# Revit family: 872-00-001-DN80-1600
name_source: partatom
category: Pipe Accessories
units: mm (PartAtom-declared; Revit-internal decimal feet)

## family parameters
Always vertical = Yes
Cut with Voids When Loaded = No
Part Type = Valve - Breaks Into
Round Connector Dimension = Use Diameter
Shared = No
Work Plane-Based = No

## types (33) — shared parameters
Body_wallthickness = 10 mm  [stored 0.0328084 ft]
DN080_PN10/16 = 872-0080-00-10900100100
DN1000_PN10 = 872-1000-00-00100100000
DN1000_PN16 = 872-1000-00-10100100000
DN100_PN10/16 = 872-0100-00-10900100100
DN1200_PN10 = 872-1200-00-00100100000
DN1200_PN16 = 872-1200-00-10100100000
DN1400_PN10 = 872-1400-00-00100100000
DN1400_PN16 = 872-1400-00-10100100000
DN150_PN10/16 = 872-0150-00-10900100100
DN1600_PN10 = 872-1600-00-00100100000
DN1600_PN16 = 872-1600-00-10100100000
DN200_PN10 = 872-0200-00-00100100000
DN200_PN16 = 872-0200-00-10100100000
DN250_PN10 = 872-0250-00-00100100000
DN250_PN16 = 872-0250-00-10100100000
DN300_PN10 = 872-0300-00-00100100000
DN300_PN16 = 872-0300-00-10100100000
DN350_PN10 = 872-0350-00-00100100000
DN350_PN16 = 872-0350-00-10100100000
DN400_PN10 = 872-0400-00-00100100000
DN400_PN16 = 872-0400-00-10100100000
DN450_PN10 = 872-0450-00-00100100000
DN450_PN16 = 872-0450-00-10100100000
DN500_PN10 = 872-0500-00-00100100000
DN500_PN16 = 872-0500-00-10100100000
DN600_PN10 = 872-0600-00-00100100000
DN600_PN16 = 872-0600-00-10100100000
DN700_PN10 = 872-0700-00-00100100000
DN700_PN16 = 872-0700-00-10100100000
DN800_PN10 = 872-0800-00-00100100000
DN800_PN16 = 872-0800-00-10100100000
DN900_PN10 = 872-0900-00-00100100000
DN900_PN16 = 872-0900-00-10100100000
Description_ = AVK NEEDLE VALVE
RF_Thick = 3 mm  [stored 0.00984252 ft]
Search_Table = 872-00-001-DN80-1600
URL product pages = https://www.avkvalves.com

## per-type parameters (varying)
- DN0080_PN10/16: (A_ref+W)/2=303 mm; A=125 mm; A_ref=275 mm; B=117 mm; D=100 mm; DN=80 mm  [stored 0.262467 ft]; FOD=95 mm; FOD_ref=50 mm  [stored 0.164042 ft]; FOD_ref_2=32 mm  [stored 0.104987 ft]; Fillet_thickness=10 mm  [stored 0.0328084 ft]; Flange_thickness=19 mm  [stored 0.062336 ft]; Flange_thickness_ref=10 mm  [stored 0.0328084 ft]; Flange_thickness_ref_2=5 mm  [stored 0.0164042 ft]; H3=230 mm; H3_ref=195 mm; ID=40 mm  [stored 0.131234 ft]; ID_ref=70 mm  [stored 0.229659 ft]; ID_ref_2=35 mm  [stored 0.114829 ft]; ID_ref_3=105 mm; ID_ref_4=35 mm  [stored 0.114829 ft]; L=260 mm; L1=111 mm; L2=65 mm  [stored 0.213255 ft]; Rf_Dia=66 mm  [stored 0.216535 ft]; Ring_Dia=35 mm  [stored 0.114829 ft]; Ring_Dia_2=15 mm  [stored 0.0492126 ft]; W=330 mm
- DN0100_PN10/16: (A_ref+W)/2=334 mm; A=145 mm; A_ref=308 mm; B=117 mm; D=120 mm; DN=100 mm; FOD=110 mm; FOD_ref=60 mm  [stored 0.19685 ft]; FOD_ref_2=37 mm; Fillet_thickness=10 mm  [stored 0.0328084 ft]; Flange_thickness=19 mm  [stored 0.062336 ft]; Flange_thickness_ref=10 mm  [stored 0.0328084 ft]; Flange_thickness_ref_2=5 mm  [stored 0.0164042 ft]; H3=230 mm; H3_ref=195 mm; ID=50 mm  [stored 0.164042 ft]; ID_ref=70 mm  [stored 0.229659 ft]; ID_ref_2=35 mm  [stored 0.114829 ft]; ID_ref_3=105 mm; ID_ref_4=35 mm  [stored 0.114829 ft]; L=300 mm; L1=131 mm; L2=75 mm; Rf_Dia=78 mm  [stored 0.255906 ft]; Ring_Dia=35 mm  [stored 0.114829 ft]; Ring_Dia_2=15 mm  [stored 0.0492126 ft]; W=360 mm
- DN0150_PN10/16: (A_ref+W)/2=398 mm; A=175 mm; A_ref=371 mm; B=150 mm; D=135 mm; DN=150 mm; FOD=143 mm; FOD_ref=85 mm; FOD_ref_2=48 mm  [stored 0.15748 ft]; Fillet_thickness=10 mm  [stored 0.0328084 ft]; Flange_thickness=19 mm  [stored 0.062336 ft]; Flange_thickness_ref=10 mm  [stored 0.0328084 ft]; Flange_thickness_ref_2=5 mm  [stored 0.0164042 ft]; H3=295 mm; H3_ref=260 mm; ID=75 mm; ID_ref=70 mm  [stored 0.229659 ft]; ID_ref_2=35 mm  [stored 0.114829 ft]; ID_ref_3=105 mm; ID_ref_4=35 mm  [stored 0.114829 ft]; L=350 mm; L1=156 mm; L2=88 mm; Rf_Dia=106 mm; Ring_Dia=35 mm  [stored 0.114829 ft]; Ring_Dia_2=15 mm  [stored 0.0492126 ft]; W=425 mm
- DN0200_PN10: (A_ref+W)/2=473 mm; A=220 mm; A_ref=445 mm; B=150 mm; D=150 mm; DN=200 mm; FOD=170 mm; FOD_ref=110 mm; FOD_ref_2=57 mm; Fillet_thickness=20 mm  [stored 0.0656168 ft]; Flange_thickness=20 mm  [stored 0.0656168 ft]; Flange_thickness_ref=10 mm  [stored 0.0328084 ft]; Flange_thickness_ref_2=5 mm  [stored 0.0164042 ft]; H3=425 mm; H3_ref=380 mm; ID=100 mm; ID_ref=90 mm; ID_ref_2=45 mm  [stored 0.147638 ft]; ID_ref_3=135 mm; ID_ref_4=45 mm  [stored 0.147638 ft]; L=400 mm; L1=180 mm; L2=100 mm; Rf_Dia=133 mm; Ring_Dia=45 mm  [stored 0.147638 ft]; Ring_Dia_2=25 mm  [stored 0.082021 ft]; W=500 mm
- DN0200_PN16: (A_ref+W)/2=473 mm; A=220 mm; A_ref=445 mm; B=150 mm; D=150 mm; DN=200 mm; FOD=170 mm; FOD_ref=110 mm; FOD_ref_2=57 mm; Fillet_thickness=20 mm  [stored 0.0656168 ft]; Flange_thickness=20 mm  [stored 0.0656168 ft]; Flange_thickness_ref=10 mm  [stored 0.0328084 ft]; Flange_thickness_ref_2=5 mm  [stored 0.0164042 ft]; H3=425 mm; H3_ref=378 mm; ID=100 mm; ID_ref=95 mm; ID_ref_2=48 mm  [stored 0.15748 ft]; ID_ref_3=143 mm; ID_ref_4=48 mm  [stored 0.15748 ft]; L=400 mm; L1=180 mm; L2=100 mm; Rf_Dia=133 mm; Ring_Dia=48 mm  [stored 0.15748 ft]; Ring_Dia_2=28 mm  [stored 0.0918635 ft]; W=500 mm
- DN0250_PN10: (A_ref+W)/2=539 mm; A=260 mm; A_ref=513 mm; B=150 mm; D=165 mm; DN=250 mm; FOD=200 mm; FOD_ref=135 mm; FOD_ref_2=67 mm; Fillet_thickness=22 mm  [stored 0.0721785 ft]; Flange_thickness=22 mm  [stored 0.0721785 ft]; Flange_thickness_ref=11 mm  [stored 0.0360892 ft]; Flange_thickness_ref_2=6 mm  [stored 0.019685 ft]; H3=475 mm; H3_ref=415 mm; ID=125 mm; ID_ref=120 mm; ID_ref_2=60 mm  [stored 0.19685 ft]; ID_ref_3=180 mm; ID_ref_4=60 mm  [stored 0.19685 ft]; L=450 mm; L1=203 mm; L2=113 mm; Rf_Dia=160 mm; Ring_Dia=60 mm  [stored 0.19685 ft]; Ring_Dia_2=40 mm  [stored 0.131234 ft]; W=565 mm
- DN0250_PN16: (A_ref+W)/2=543 mm; A=260 mm; A_ref=515 mm; B=150 mm; D=165 mm; DN=250 mm; FOD=200 mm; FOD_ref=135 mm; FOD_ref_2=67 mm; Fillet_thickness=22 mm  [stored 0.0721785 ft]; Flange_thickness=22 mm  [stored 0.0721785 ft]; Flange_thickness_ref=11 mm  [stored 0.0360892 ft]; Flange_thickness_ref_2=6 mm  [stored 0.019685 ft]; H3=475 mm; H3_ref=415 mm; ID=125 mm; ID_ref=120 mm; ID_ref_2=60 mm  [stored 0.19685 ft]; ID_ref_3=180 mm; ID_ref_4=60 mm  [stored 0.19685 ft]; L=450 mm; L1=203 mm; L2=113 mm; Rf_Dia=160 mm; Ring_Dia=60 mm  [stored 0.19685 ft]; Ring_Dia_2=40 mm  [stored 0.131234 ft]; W=570 mm
- DN0300_PN10: (A_ref+W)/2=624 mm; A=305 mm; A_ref=594 mm; B=155 mm; D=185 mm; DN=300 mm; FOD=228 mm; FOD_ref=160 mm; FOD_ref_2=76 mm; Fillet_thickness=25 mm  [stored 0.082021 ft]; Flange_thickness=25 mm  [stored 0.082021 ft]; Flange_thickness_ref=12 mm  [stored 0.0393701 ft]; Flange_thickness_ref_2=6 mm  [stored 0.019685 ft]; H3=535 mm; H3_ref=470 mm; ID=150 mm; ID_ref=130 mm; ID_ref_2=65 mm  [stored 0.213255 ft]; ID_ref_3=195 mm; ID_ref_4=65 mm  [stored 0.213255 ft]; L=500 mm; L1=226 mm; L2=125 mm; Rf_Dia=185 mm; Ring_Dia=65 mm  [stored 0.213255 ft]; Ring_Dia_2=45 mm  [stored 0.147638 ft]; W=655 mm
- DN0300_PN16: (A_ref+W)/2=624 mm; A=305 mm; A_ref=594 mm; B=155 mm; D=185 mm; DN=300 mm; FOD=228 mm; FOD_ref=160 mm; FOD_ref_2=76 mm; Fillet_thickness=25 mm  [stored 0.082021 ft]; Flange_thickness=25 mm  [stored 0.082021 ft]; Flange_thickness_ref=12 mm  [stored 0.0393701 ft]; Flange_thickness_ref_2=6 mm  [stored 0.019685 ft]; H3=535 mm; H3_ref=470 mm; ID=150 mm; ID_ref=130 mm; ID_ref_2=65 mm  [stored 0.213255 ft]; ID_ref_3=195 mm; ID_ref_4=65 mm  [stored 0.213255 ft]; L=500 mm; L1=226 mm; L2=125 mm; Rf_Dia=185 mm; Ring_Dia=65 mm  [stored 0.213255 ft]; Ring_Dia_2=45 mm  [stored 0.147638 ft]; W=655 mm
- DN0350_PN10: (A_ref+W)/2=691 mm; A=345 mm; A_ref=663 mm; B=170 mm; D=205 mm; DN=350 mm; FOD=260 mm; FOD_ref=185 mm; FOD_ref_2=87 mm; Fillet_thickness=27 mm; Flange_thickness=27 mm; Flange_thickness_ref=13 mm; Flange_thickness_ref_2=7 mm  [stored 0.0229659 ft]; H3=595 mm; H3_ref=520 mm; ID=175 mm; ID_ref=150 mm; ID_ref_2=75 mm; ID_ref_3=225 mm; ID_ref_4=75 mm; L=550 mm; L1=249 mm; L2=138 mm; Rf_Dia=215 mm; Ring_Dia=75 mm; Ring_Dia_2=55 mm  [stored 0.180446 ft]; W=720 mm
- DN0350_PN16: (A_ref+W)/2=695 mm; A=345 mm; A_ref=665 mm; B=170 mm; D=205 mm; DN=350 mm; FOD=260 mm; FOD_ref=185 mm; FOD_ref_2=87 mm; Fillet_thickness=27 mm; Flange_thickness=27 mm; Flange_thickness_ref=13 mm; Flange_thickness_ref_2=7 mm  [stored 0.0229659 ft]; H3=595 mm; H3_ref=520 mm; ID=175 mm; ID_ref=150 mm; ID_ref_2=75 mm; ID_ref_3=225 mm; ID_ref_4=75 mm; L=550 mm; L1=249 mm; L2=138 mm; Rf_Dia=215 mm; Ring_Dia=75 mm; Ring_Dia_2=55 mm  [stored 0.180446 ft]; W=725 mm
- DN0400_PN10: (A_ref+W)/2=788 mm; A=385 mm; A_ref=750 mm; B=300 mm; D=235 mm; DN=400 mm; FOD=290 mm; FOD_ref=210 mm; FOD_ref_2=97 mm; Fillet_thickness=28 mm  [stored 0.0918635 ft]; Flange_thickness=28 mm  [stored 0.0918635 ft]; Flange_thickness_ref=14 mm  [stored 0.0459318 ft]; Flange_thickness_ref_2=7 mm  [stored 0.0229659 ft]; H3=660 mm; H3_ref=585 mm; ID=200 mm; ID_ref=150 mm; ID_ref_2=75 mm; ID_ref_3=225 mm; ID_ref_4=75 mm; L=600 mm; L1=272 mm; L2=150 mm; Rf_Dia=240 mm; Ring_Dia=75 mm; Ring_Dia_2=55 mm  [stored 0.180446 ft]; W=825 mm
- DN0400_PN16: (A_ref+W)/2=788 mm; A=385 mm; A_ref=750 mm; B=300 mm; D=235 mm; DN=400 mm; FOD=290 mm; FOD_ref=210 mm; FOD_ref_2=97 mm; Fillet_thickness=28 mm  [stored 0.0918635 ft]; Flange_thickness=28 mm  [stored 0.0918635 ft]; Flange_thickness_ref=14 mm  [stored 0.0459318 ft]; Flange_thickness_ref_2=7 mm  [stored 0.0229659 ft]; H3=660 mm; H3_ref=585 mm; ID=200 mm; ID_ref=150 mm; ID_ref_2=75 mm; ID_ref_3=225 mm; ID_ref_4=75 mm; L=600 mm; L1=272 mm; L2=150 mm; Rf_Dia=240 mm; Ring_Dia=75 mm; Ring_Dia_2=55 mm  [stored 0.180446 ft]; W=825 mm
- DN0450_PN10: (A_ref+W)/2=840 mm; A=415 mm; A_ref=805 mm; B=300 mm; D=240 mm; DN=450 mm; FOD=320 mm; FOD_ref=235 mm; FOD_ref_2=107 mm; Fillet_thickness=30 mm  [stored 0.0984252 ft]; Flange_thickness=30 mm  [stored 0.0984252 ft]; Flange_thickness_ref=15 mm  [stored 0.0492126 ft]; Flange_thickness_ref_2=8 mm  [stored 0.0262467 ft]; H3=745 mm; H3_ref=670 mm; ID=225 mm; ID_ref=150 mm; ID_ref_2=75 mm; ID_ref_3=225 mm; ID_ref_4=75 mm; L=650 mm; L1=295 mm; L2=163 mm; Rf_Dia=274 mm; Ring_Dia=75 mm; Ring_Dia_2=55 mm  [stored 0.180446 ft]; W=875 mm
- DN0450_PN16: (A_ref+W)/2=848 mm; A=415 mm; A_ref=810 mm; B=300 mm; D=240 mm; DN=450 mm; FOD=320 mm; FOD_ref=235 mm; FOD_ref_2=107 mm; Fillet_thickness=30 mm  [stored 0.0984252 ft]; Flange_thickness=30 mm  [stored 0.0984252 ft]; Flange_thickness_ref=15 mm  [stored 0.0492126 ft]; Flange_thickness_ref_2=8 mm  [stored 0.0262467 ft]; H3=745 mm; H3_ref=670 mm; ID=225 mm; ID_ref=150 mm; ID_ref_2=75 mm; ID_ref_3=225 mm; ID_ref_4=75 mm; L=650 mm; L1=295 mm; L2=163 mm; Rf_Dia=274 mm; Ring_Dia=75 mm; Ring_Dia_2=55 mm  [stored 0.180446 ft]; W=885 mm
- DN0500_PN10: (A_ref+W)/2=902 mm; A=445 mm; A_ref=869 mm; B=300 mm; D=245 mm; DN=500 mm; FOD=358 mm; FOD_ref=260 mm; FOD_ref_2=119 mm; Fillet_thickness=32 mm  [stored 0.104987 ft]; Flange_thickness=32 mm  [stored 0.104987 ft]; Flange_thickness_ref=16 mm; Flange_thickness_ref_2=8 mm  [stored 0.0262467 ft]; H3=785 mm; H3_ref=710 mm; ID=250 mm; ID_ref=150 mm; ID_ref_2=75 mm; ID_ref_3=225 mm; ID_ref_4=75 mm; L=700 mm; L1=319 mm; L2=175 mm; Rf_Dia=291 mm; Ring_Dia=75 mm; Ring_Dia_2=55 mm  [stored 0.180446 ft]; W=935 mm
- DN0500_PN16: (A_ref+W)/2=913 mm; A=445 mm; A_ref=876 mm; B=300 mm; D=245 mm; DN=500 mm; FOD=358 mm; FOD_ref=260 mm; FOD_ref_2=119 mm; Fillet_thickness=32 mm  [stored 0.104987 ft]; Flange_thickness=32 mm  [stored 0.104987 ft]; Flange_thickness_ref=16 mm; Flange_thickness_ref_2=8 mm  [stored 0.0262467 ft]; H3=785 mm; H3_ref=710 mm; ID=250 mm; ID_ref=150 mm; ID_ref_2=75 mm; ID_ref_3=225 mm; ID_ref_4=75 mm; L=700 mm; L1=319 mm; L2=175 mm; Rf_Dia=291 mm; Ring_Dia=75 mm; Ring_Dia_2=55 mm  [stored 0.180446 ft]; W=950 mm
- DN0600_PN10: (A_ref+W)/2=1026 mm; A=505 mm; A_ref=993 mm; B=300 mm; D=280 mm; DN=600 mm; FOD=420 mm; FOD_ref=310 mm; FOD_ref_2=140 mm; Fillet_thickness=36 mm  [stored 0.11811 ft]; Flange_thickness=36 mm  [stored 0.11811 ft]; Flange_thickness_ref=18 mm  [stored 0.0590551 ft]; Flange_thickness_ref_2=9 mm  [stored 0.0295276 ft]; H3=925 mm; H3_ref=845 mm; ID=300 mm; ID_ref=160 mm; ID_ref_2=80 mm  [stored 0.262467 ft]; ID_ref_3=240 mm; ID_ref_4=80 mm  [stored 0.262467 ft]; L=800 mm; L1=364 mm; L2=200 mm; Rf_Dia=360 mm; Ring_Dia=80 mm  [stored 0.262467 ft]; Ring_Dia_2=60 mm  [stored 0.19685 ft]; W=1060 mm
- DN0600_PN16: (A_ref+W)/2=1034 mm; A=505 mm; A_ref=998 mm; B=300 mm; D=280 mm; DN=600 mm; FOD=420 mm; FOD_ref=310 mm; FOD_ref_2=140 mm; Fillet_thickness=36 mm  [stored 0.11811 ft]; Flange_thickness=36 mm  [stored 0.11811 ft]; Flange_thickness_ref=18 mm  [stored 0.0590551 ft]; Flange_thickness_ref_2=9 mm  [stored 0.0295276 ft]; H3=925 mm; H3_ref=845 mm; ID=300 mm; ID_ref=160 mm; ID_ref_2=80 mm  [stored 0.262467 ft]; ID_ref_3=240 mm; ID_ref_4=80 mm  [stored 0.262467 ft]; L=800 mm; L1=364 mm; L2=200 mm; Rf_Dia=360 mm; Ring_Dia=80 mm  [stored 0.262467 ft]; Ring_Dia_2=60 mm  [stored 0.19685 ft]; W=1070 mm
- DN0700_PN10: (A_ref+W)/2=1142 mm; A=565 mm; A_ref=1099 mm; B=305 mm; D=315 mm; DN=700 mm; FOD=448 mm; FOD_ref=360 mm; FOD_ref_2=149 mm; Fillet_thickness=40 mm  [stored 0.131234 ft]; Flange_thickness=40 mm  [stored 0.131234 ft]; Flange_thickness_ref=20 mm  [stored 0.0656168 ft]; Flange_thickness_ref_2=10 mm  [stored 0.0328084 ft]; H3=1045 mm; H3_ref=965 mm; ID=350 mm; ID_ref=160 mm; ID_ref_2=80 mm  [stored 0.262467 ft]; ID_ref_3=240 mm; ID_ref_4=80 mm  [stored 0.262467 ft]; L=900 mm; L1=410 mm; L2=225 mm; Rf_Dia=397 mm; Ring_Dia=80 mm  [stored 0.262467 ft]; Ring_Dia_2=60 mm  [stored 0.19685 ft]; W=1185 mm
- DN0700_PN16: (A_ref+W)/2=1144 mm; A=565 mm; A_ref=1103 mm; B=305 mm; D=315 mm; DN=700 mm; FOD=455 mm; FOD_ref=360 mm; FOD_ref_2=152 mm; Fillet_thickness=40 mm  [stored 0.131234 ft]; Flange_thickness=40 mm  [stored 0.131234 ft]; Flange_thickness_ref=20 mm  [stored 0.0656168 ft]; Flange_thickness_ref_2=10 mm  [stored 0.0328084 ft]; H3=1045 mm; H3_ref=965 mm; ID=350 mm; ID_ref=160 mm; ID_ref_2=80 mm  [stored 0.262467 ft]; ID_ref_3=240 mm; ID_ref_4=80 mm  [stored 0.262467 ft]; L=900 mm; L1=410 mm; L2=225 mm; Rf_Dia=397 mm; Ring_Dia=80 mm  [stored 0.262467 ft]; Ring_Dia_2=60 mm  [stored 0.19685 ft]; W=1185 mm
- DN0800_PN10: (A_ref+W)/2=1291 mm; A=650 mm; A_ref=1246 mm; B=305 mm; D=350 mm; DN=800 mm; FOD=508 mm; FOD_ref=410 mm; FOD_ref_2=169 mm; Fillet_thickness=40 mm  [stored 0.131234 ft]; Flange_thickness=40 mm  [stored 0.131234 ft]; Flange_thickness_ref=20 mm  [stored 0.0656168 ft]; Flange_thickness_ref_2=10 mm  [stored 0.0328084 ft]; H3=1180 mm; H3_ref=1100 mm; ID=400 mm; ID_ref=160 mm; ID_ref_2=80 mm  [stored 0.262467 ft]; ID_ref_3=240 mm; ID_ref_4=80 mm  [stored 0.262467 ft]; L=1000 mm; L1=460 mm; L2=250 mm; Rf_Dia=450 mm; Ring_Dia=80 mm  [stored 0.262467 ft]; Ring_Dia_2=60 mm  [stored 0.19685 ft]; W=1335 mm
- DN0800_PN16: (A_ref+W)/2=1291 mm; A=650 mm; A_ref=1246 mm; B=335 mm; D=350 mm; DN=801 mm; FOD=508 mm; FOD_ref=411 mm; FOD_ref_2=169 mm; Fillet_thickness=40 mm  [stored 0.131234 ft]; Flange_thickness=40 mm  [stored 0.131234 ft]; Flange_thickness_ref=20 mm  [stored 0.0656168 ft]; Flange_thickness_ref_2=10 mm  [stored 0.0328084 ft]; H3=1180 mm; H3_ref=1100 mm; ID=401 mm; ID_ref=160 mm; ID_ref_2=80 mm  [stored 0.262467 ft]; ID_ref_3=240 mm; ID_ref_4=80 mm  [stored 0.262467 ft]; L=1000 mm; L1=460 mm; L2=250 mm; Rf_Dia=450 mm; Ring_Dia=80 mm  [stored 0.262467 ft]; Ring_Dia_2=60 mm  [stored 0.19685 ft]; W=1335 mm
- DN0900_PN10: (A_ref+W)/2=1398 mm; A=715 mm; A_ref=1356 mm; B=335 mm; D=385 mm; DN=900 mm; FOD=558 mm; FOD_ref=460 mm; FOD_ref_2=186 mm; Fillet_thickness=40 mm  [stored 0.131234 ft]; Flange_thickness=40 mm  [stored 0.131234 ft]; Flange_thickness_ref=20 mm  [stored 0.0656168 ft]; Flange_thickness_ref_2=10 mm  [stored 0.0328084 ft]; H3=1320 mm; H3_ref=1235 mm; ID=450 mm; ID_ref=170 mm; ID_ref_2=85 mm; ID_ref_3=255 mm; ID_ref_4=85 mm; L=1100 mm; L1=510 mm; L2=275 mm; Rf_Dia=500 mm; Ring_Dia=85 mm; Ring_Dia_2=65 mm  [stored 0.213255 ft]; W=1440 mm
- DN0900_PN16: (A_ref+W)/2=1398 mm; A=715 mm; A_ref=1356 mm; B=335 mm; D=385 mm; DN=900 mm; FOD=558 mm; FOD_ref=460 mm; FOD_ref_2=186 mm; Fillet_thickness=40 mm  [stored 0.131234 ft]; Flange_thickness=40 mm  [stored 0.131234 ft]; Flange_thickness_ref=20 mm  [stored 0.0656168 ft]; Flange_thickness_ref_2=10 mm  [stored 0.0328084 ft]; H3=1320 mm; H3_ref=1235 mm; ID=450 mm; ID_ref=170 mm; ID_ref_2=85 mm; ID_ref_3=255 mm; ID_ref_4=85 mm; L=1100 mm; L1=510 mm; L2=275 mm; Rf_Dia=500 mm; Ring_Dia=85 mm; Ring_Dia_2=65 mm  [stored 0.213255 ft]; W=1440 mm
- DN1000_PN10: (A_ref+W)/2=1536 mm; A=760 mm; A_ref=1483 mm; B=510 mm; D=400 mm; DN=1000 mm; FOD=615 mm; FOD_ref=510 mm; FOD_ref_2=205 mm; Fillet_thickness=40 mm  [stored 0.131234 ft]; Flange_thickness=40 mm  [stored 0.131234 ft]; Flange_thickness_ref=20 mm  [stored 0.0656168 ft]; Flange_thickness_ref_2=10 mm  [stored 0.0328084 ft]; H3=1490 mm; H3_ref=1400 mm; ID=500 mm; ID_ref=180 mm; ID_ref_2=90 mm; ID_ref_3=270 mm; ID_ref_4=90 mm; L=1200 mm; L1=560 mm; L2=300 mm; Rf_Dia=556 mm; Ring_Dia=90 mm; Ring_Dia_2=70 mm  [stored 0.229659 ft]; W=1590 mm
- DN1000_PN16: (A_ref+W)/2=1536 mm; A=760 mm; A_ref=1483 mm; B=510 mm; D=400 mm; DN=1000 mm; FOD=615 mm; FOD_ref=510 mm; FOD_ref_2=205 mm; Fillet_thickness=40 mm  [stored 0.131234 ft]; Flange_thickness=40 mm  [stored 0.131234 ft]; Flange_thickness_ref=20 mm  [stored 0.0656168 ft]; Flange_thickness_ref_2=10 mm  [stored 0.0328084 ft]; H3=1490 mm; H3_ref=1400 mm; ID=500 mm; ID_ref=180 mm; ID_ref_2=90 mm; ID_ref_3=270 mm; ID_ref_4=90 mm; L=1200 mm; L1=560 mm; L2=300 mm; Rf_Dia=556 mm; Ring_Dia=90 mm; Ring_Dia_2=70 mm  [stored 0.229659 ft]; W=1590 mm
- DN1200_PN10: (A_ref+W)/2=1757 mm; A=870 mm; A_ref=1704 mm; B=510 mm; D=415 mm; DN=1200 mm; FOD=728 mm; FOD_ref=610 mm; FOD_ref_2=243 mm; Fillet_thickness=40 mm  [stored 0.131234 ft]; Flange_thickness=40 mm  [stored 0.131234 ft]; Flange_thickness_ref=20 mm  [stored 0.0656168 ft]; Flange_thickness_ref_2=10 mm  [stored 0.0328084 ft]; H3=1710 mm; H3_ref=1620 mm; ID=600 mm; ID_ref=180 mm; ID_ref_2=90 mm; ID_ref_3=270 mm; ID_ref_4=90 mm; L=1400 mm; L1=660 mm; L2=350 mm; Rf_Dia=666 mm; Ring_Dia=90 mm; Ring_Dia_2=70 mm  [stored 0.229659 ft]; W=1810 mm
- DN1200_PN16: (A_ref+W)/2=1761 mm; A=870 mm; A_ref=1711 mm; B=510 mm; D=415 mm; DN=1200 mm; FOD=743 mm; FOD_ref=610 mm; FOD_ref_2=248 mm; Fillet_thickness=50 mm  [stored 0.164042 ft]; Flange_thickness=50 mm  [stored 0.164042 ft]; Flange_thickness_ref=25 mm  [stored 0.082021 ft]; Flange_thickness_ref_2=13 mm; H3=1710 mm; H3_ref=1620 mm; ID=600 mm; ID_ref=180 mm; ID_ref_2=90 mm; ID_ref_3=270 mm; ID_ref_4=90 mm; L=1400 mm; L1=650 mm; L2=350 mm; Rf_Dia=666 mm; Ring_Dia=90 mm; Ring_Dia_2=70 mm  [stored 0.229659 ft]; W=1810 mm
- DN1400_PN10: (A_ref+W)/2=2034 mm; A=1000 mm; A_ref=1969 mm; B=510 mm; D=480 mm; DN=1400 mm; FOD=838 mm; FOD_ref=710 mm; FOD_ref_2=279 mm; Fillet_thickness=50 mm  [stored 0.164042 ft]; Flange_thickness=50 mm  [stored 0.164042 ft]; Flange_thickness_ref=25 mm  [stored 0.082021 ft]; Flange_thickness_ref_2=13 mm; H3=1960 mm; H3_ref=1865 mm; ID=700 mm; ID_ref=190 mm; ID_ref_2=95 mm; ID_ref_3=285 mm; ID_ref_4=95 mm; L=1600 mm; L1=750 mm; L2=400 mm; Rf_Dia=763 mm; Ring_Dia=95 mm; Ring_Dia_2=75 mm; W=2100 mm
- DN1400_PN16: (A_ref+W)/2=2036 mm; A=1000 mm; A_ref=1971 mm; B=610 mm; D=480 mm; DN=1400 mm; FOD=843 mm; FOD_ref=710 mm; FOD_ref_2=281 mm; Fillet_thickness=50 mm  [stored 0.164042 ft]; Flange_thickness=50 mm  [stored 0.164042 ft]; Flange_thickness_ref=25 mm  [stored 0.082021 ft]; Flange_thickness_ref_2=13 mm; H3=1960 mm; H3_ref=1865 mm; ID=700 mm; ID_ref=190 mm; ID_ref_2=95 mm; ID_ref_3=285 mm; ID_ref_4=95 mm; L=1600 mm; L1=750 mm; L2=400 mm; Rf_Dia=763 mm; Ring_Dia=95 mm; Ring_Dia_2=75 mm; W=2100 mm
- DN1600_PN10: (A_ref+W)/2=2358 mm; A=1153 mm; A_ref=2275 mm; B=610 mm; D=625 mm; DN=1600 mm; FOD=958 mm; FOD_ref=810 mm; FOD_ref_2=319 mm; Fillet_thickness=50 mm  [stored 0.164042 ft]; Flange_thickness=50 mm  [stored 0.164042 ft]; Flange_thickness_ref=25 mm  [stored 0.082021 ft]; Flange_thickness_ref_2=13 mm; H3=2230 mm; H3_ref=2135 mm; ID=800 mm; ID_ref=190 mm; ID_ref_2=95 mm; ID_ref_3=285 mm; ID_ref_4=95 mm; L=1800 mm; L1=850 mm; L2=450 mm; Rf_Dia=875 mm; Ring_Dia=95 mm; Ring_Dia_2=75 mm; W=2440 mm
- DN1600_PN16: (A_ref+W)/2=2360 mm; A=1153 mm; A_ref=2279 mm; B=741 mm; D=625 mm; DN=1600 mm; FOD=965 mm; FOD_ref=810 mm; FOD_ref_2=322 mm; Fillet_thickness=60 mm  [stored 0.19685 ft]; Flange_thickness=60 mm  [stored 0.19685 ft]; Flange_thickness_ref=30 mm  [stored 0.0984252 ft]; Flange_thickness_ref_2=15 mm  [stored 0.0492126 ft]; H3=2230 mm; H3_ref=2135 mm; ID=800 mm; ID_ref=190 mm; ID_ref_2=95 mm; ID_ref_3=285 mm; ID_ref_4=95 mm; L=1800 mm; L1=840 mm; L2=450 mm; Rf_Dia=875 mm; Ring_Dia=95 mm; Ring_Dia_2=75 mm; W=2440 mm

note: [stored X ft] marks values corroborated as IEEE doubles in the binary element streams (Revit-internal decimal feet)

## geometry (parser evidence)
native form markers: Sweep x14
no freeform markers — native parametric forms only
